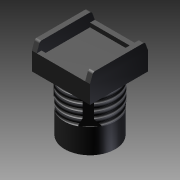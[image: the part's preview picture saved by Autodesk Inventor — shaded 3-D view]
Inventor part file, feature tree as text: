
AUTODESK INVENTOR PART (.ipt)
format: ipt  version: 2014 (Build 180170000, 170)  size: 213,504 bytes
history: native  units: in
note: dims shown in document units (in); Inventor stores cm internally (conversion verified against a paired STEP export)
features: sketch x11, extrude x9, revolve x2, thread x1
ambient origin geometry x8: Origin, YZ Plane, XZ Plane, XY Plane, X Axis, Y Axis, Z Axis, Center Point
bodies: Solid1 (feature_tree), body_to_cap_XY (feature_tree), body_to_cap_YZ (feature_tree), body_to_cap_ZX (feature_tree), body_to_cap_X (feature_tree), body_to_cap_Y (feature_tree), body_to_cap_Z (feature_tree), body_to_cap_Center (feature_tree), body_to_metal_XY (feature_tree), body_to_metal_YZ (feature_tree), body_to_metal_ZX (feature_tree), body_to_metal_X (feature_tree), body_to_metal_Y (feature_tree), body_to_metal_Z (feature_tree), body_to_metal_Center (feature_tree), body_to_nut_XY (feature_tree), body_to_nut_YZ (feature_tree), body_to_nut_ZX (feature_tree), body_to_nut_X (feature_tree), body_to_nut_Y (feature_tree), body_to_nut_Z (feature_tree), body_to_nut_Center (feature_tree)
feature tree (23):
  revolve  "Revolution1"  [1 undecoded]
  thread  "Thread1"  [1 undecoded]
  revolve  "Revolution2"  [1 undecoded]
  extrude  "Extrusion1"  Depth=0.02in TaperAngle=0.0deg
  extrude  "Extrusion2"  Depth=0.709in TaperAngle=0.0deg
  extrude  "Extrusion3"  Depth=0.327in TaperAngle=0.0deg
  extrude  "Extrusion4"  [1 undecoded]
  extrude  "Extrusion5"  [1 undecoded]
  extrude  "Extrusion6"  [1 undecoded]
  extrude  "Extrusion7"  [1 undecoded]
  extrude  "Extrusion8"  [1 undecoded]
  extrude  "Extrusion9"  [1 undecoded]
  sketch  "Sketch_1"  dims[d0=360.0deg d1=0.337in d2=0.0in d3=360.0deg]
  sketch  "Sketch_15"
  sketch  "Sketch_7"  dims[d8=0.02in d9=0.0in d10=0.02in d11=0.0in]
  sketch  "Sketch_9"  dims[d16=1.182in d17=0.0in d18=0.327in d19=0.0in]
  sketch  "Sketch_8"  dims[d12=0.02in d13=0.0in d14=0.709in d15=0.0in]
  sketch  "Sketch_10"  dims[d20=0.1024in d21=0.0in]
  sketch  "Sketch_14"
  sketch  "Sketch_20"
  sketch  "Sketch_19"
  sketch  "Sketch_18"
  sketch  "Sketch_2"  dims[d4=0.02in d5=0.0in d6=0.02in d7=0.0in]
note: 9 required parameter values undecoded (feature->parameter linkage not recoverable at this tier; creation-order binding heuristic only, values carry confidence <= 0.55)